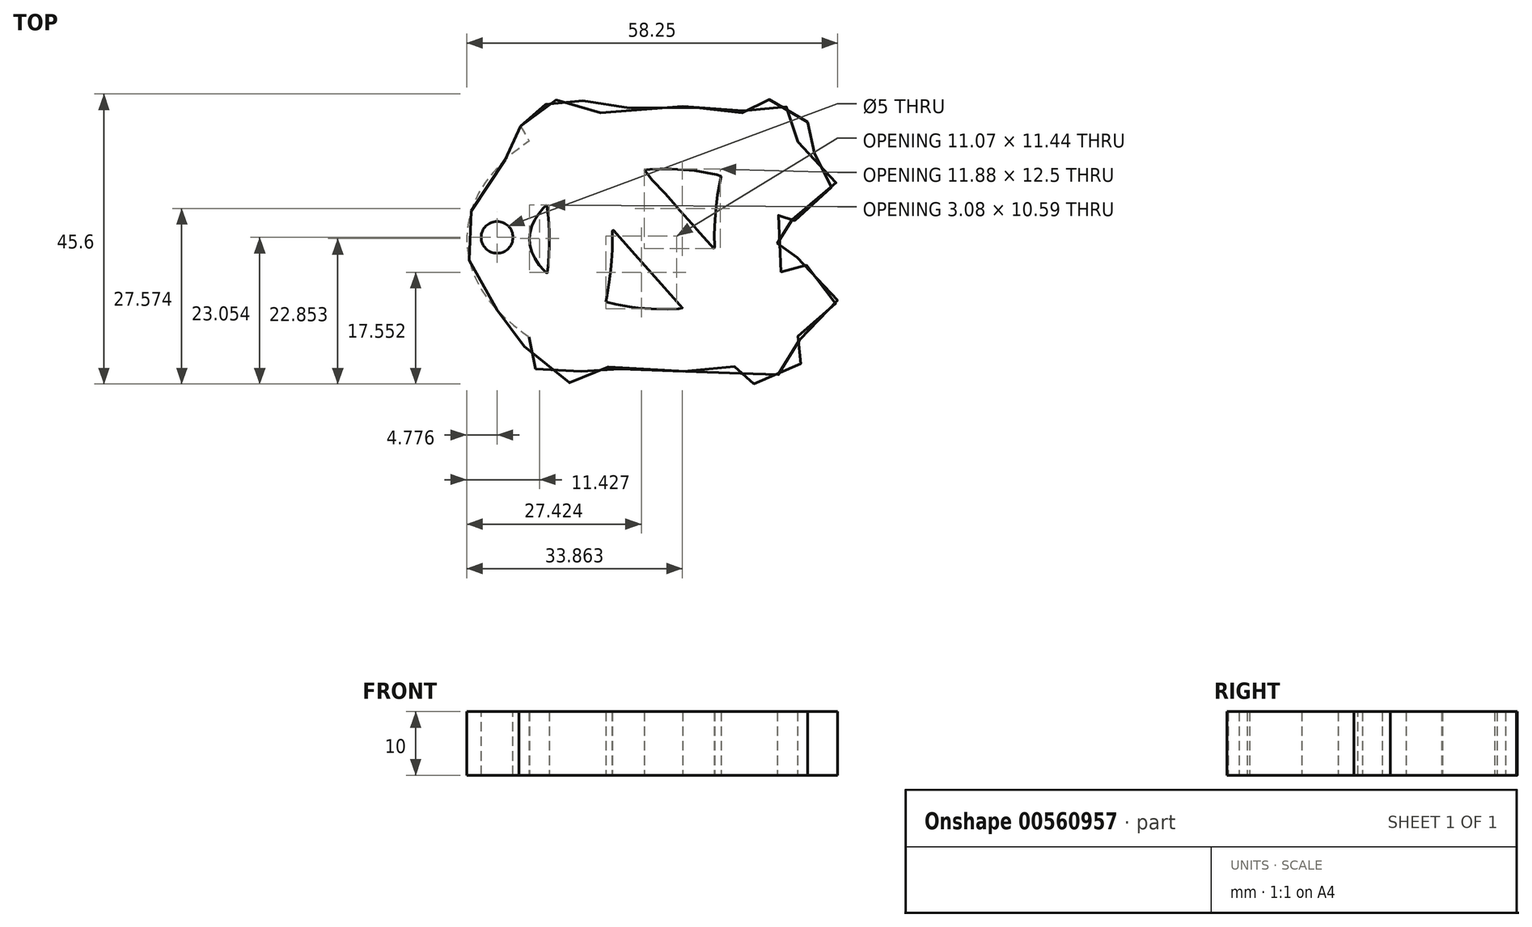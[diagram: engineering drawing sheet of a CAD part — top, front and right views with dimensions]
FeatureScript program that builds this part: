
annotation { "Feature Type Name" : "Feature", "Feature Type Description" : "" }
export const myFeature = defineFeature(function(context is Context, id is Id, definition is map)
    precondition{}
    {
        {
            var Q0;
            Q0=qCreatedBy(makeId("Top.planeOp"),FACE);
            var sketch = newSketch(context, id + "F0", { "sketchPlane" : qUnion([Q0])});
            skFitSpline(sketch, "E0", {"points": [v(22.56, 13.6) * mm, v(24.28, 13.2) * mm, v(26.83, 12.77) * mm, v(28.02, 12.64) * mm, v(32.02, 12.47) * mm, v(34.06, 12.57) * mm, v(34.53, 12.6) * mm, v(34.59, 12.65) * mm, v(34.37, 12.87) * mm, v(33.38, 13.98) * mm, v(32.2, 15.3) * mm, v(29.76, 18.07) * mm, v(28.72, 19.23) * mm, v(25.85, 22.49) * mm, v(23.63, 25) * mm, v(23.56, 25.06) * mm, v(23.51, 24.96) * mm, v(23.54, 24.73) * mm, v(23.53, 23.34) * mm, v(23.51, 21.7) * mm, v(23.39, 19.63) * mm, v(23.28, 18.47) * mm, v(22.87, 15.57) * mm, v(22.57, 13.83) * mm, v(22.56, 13.6) * mm]});
            skFitSpline(sketch, "E1", {"points": [v(28.6, 34.36) * mm, v(31.72, 30.78) * mm, v(32.9, 29.45) * mm, v(36.42, 25.48) * mm, v(37.9, 23.8) * mm, v(39.45, 22.04) * mm, v(39.53, 21.98) * mm, v(39.59, 21.98) * mm, v(39.59, 22.3) * mm, v(39.61, 25.62) * mm, v(39.91, 29.35) * mm, v(40.25, 31.57) * mm, v(40.6, 33.32) * mm, v(40.62, 33.43) * mm, v(40.24, 33.55) * mm, v(38.05, 34) * mm, v(35.63, 34.33) * mm, v(32.77, 34.53) * mm, v(30.36, 34.5) * mm, v(28.87, 34.45) * mm, v(28.6, 34.36) * mm]});
            skFitSpline(sketch, "E2", {"points": [v(9.14, 41.25) * mm, v(9.4, 40.84) * mm, v(9.78, 40.16) * mm, v(10.08, 39.61) * mm, v(10.38, 39) * mm, v(10.46, 38.86) * mm, v(10.35, 38.74) * mm, v(9.58, 38.22) * mm, v(8.8, 37.67) * mm, v(8, 37.07) * mm, v(6.93, 36.15) * mm, v(5.98, 35.25) * mm, v(4.6, 33.73) * mm, v(3.85, 32.8) * mm, v(3.18, 31.77) * mm, v(2.49, 30.58) * mm, v(2.03, 29.64) * mm, v(1.61, 28.58) * mm, v(1.18, 27.26) * mm, v(0.97, 26.42) * mm, v(0.77, 25.13) * mm, v(0.7, 24.4) * mm, v(0.7, 23.98) * mm, v(0.68, 23.85) * mm, v(0.7, 22.98) * mm, v(0.83, 21.5) * mm, v(0.9, 21.07) * mm, v(1.03, 20.32) * mm, v(1.38, 19.08) * mm, v(1.69, 18.25) * mm, v(2.12, 17.17) * mm, v(2.93, 15.65) * mm, v(3.38, 14.97) * mm, v(3.72, 14.43) * mm, v(4.53, 13.38) * mm, v(5.37, 12.41) * mm, v(6.6, 11.18) * mm, v(7.7, 10.2) * mm, v(8.13, 9.89) * mm, v(9.12, 9.1) * mm, v(9.74, 8.67) * mm, v(10.36, 8.29) * mm, v(10.47, 8.2) * mm, v(10.3, 7.85) * mm, v(9.98, 7.16) * mm, v(9.34, 6) * mm, v(9.03, 5.52) * mm, v(8.91, 5.1) * mm, v(9.06, 4.58) * mm, v(9.41, 4.23) * mm, v(12.7, 2.54) * mm, v(15.19, 1.49) * mm, v(16.83, 0.9) * mm, v(17.28, 0.92) * mm, v(17.6, 1.03) * mm, v(18.14, 1.78) * mm, v(18.92, 3.2) * mm, v(19.38, 4.2) * mm, v(19.41, 4.26) * mm, v(20.55, 3.92) * mm, v(21.12, 3.8) * mm, v(21.62, 3.7) * mm, v(23.49, 3.3) * mm, v(25.4, 3) * mm, v(29.12, 2.65) * mm, v(30.07, 2.6) * mm, v(32.43, 2.58) * mm, v(34.36, 2.67) * mm, v(35.25, 2.74) * mm, v(37.84, 3.02) * mm, v(40.53, 3.48) * mm, v(42.25, 3.86) * mm, v(42.32, 3.88) * mm, v(42.4, 3.84) * mm, v(42.44, 3.76) * mm, v(42.72, 3.48) * mm, v(42.85, 3.32) * mm, v(43.36, 2.75) * mm, v(43.5, 2.59) * mm, v(43.93, 2.1) * mm, v(44.09, 1.92) * mm, v(44.61, 1.35) * mm, v(44.81, 1.12) * mm, v(45, 0.92) * mm, v(45.24, 0.78) * mm, v(45.53, 0.7) * mm, v(45.85, 0.76) * mm, v(46.58, 1) * mm, v(47.24, 1.23) * mm, v(47.49, 1.32) * mm, v(49.43, 2.1) * mm, v(50.83, 2.72) * mm, v(53.05, 3.86) * mm, v(53.77, 4.28) * mm, v(54.01, 4.5) * mm, v(54.18, 4.84) * mm, v(54.16, 5.35) * mm, v(53.91, 5.82) * mm, v(53.43, 6.64) * mm, v(53.05, 7.36) * mm, v(52.67, 8.13) * mm, v(52.64, 8.17) * mm, v(53.65, 8.84) * mm, v(55.08, 9.91) * mm, v(56.03, 10.69) * mm, v(57.17, 11.77) * mm, v(57.97, 12.6) * mm, v(58.73, 13.52) * mm, v(58.91, 13.95) * mm, v(58.87, 14.37) * mm, v(58.45, 14.94) * mm, v(57.08, 16.3) * mm, v(55.6, 17.78) * mm, v(53.86, 19.52) * mm, v(53.23, 20.14) * mm, v(52.87, 20.48) * mm, v(52.82, 20.55) * mm, v(52.21, 20.64) * mm, v(51.84, 20.48) * mm, v(51.48, 20.12) * mm, v(51.12, 19.55) * mm, v(50.48, 18.8) * mm, v(49.87, 18.19) * mm, v(49.8, 18.16) * mm, v(49.77, 18.58) * mm, v(49.65, 19.88) * mm, v(49.48, 22.42) * mm, v(49.53, 25.99) * mm, v(49.73, 28.15) * mm, v(49.8, 28.75) * mm, v(49.83, 28.82) * mm, v(49.92, 28.77) * mm, v(50.42, 28.26) * mm, v(50.97, 27.61) * mm, v(51.3, 27.21) * mm, v(51.5, 26.87) * mm, v(51.73, 26.59) * mm, v(52.04, 26.45) * mm, v(52.33, 26.38) * mm, v(52.76, 26.46) * mm, v(53.26, 26.9) * mm, v(54.49, 28.12) * mm, v(54.9, 28.55) * mm, v(56.6, 30.25) * mm, v(58.22, 31.9) * mm, v(58.73, 32.4) * mm, v(58.9, 32.8) * mm, v(58.86, 33.21) * mm, v(58.04, 34.31) * mm, v(57.32, 35.1) * mm, v(56.05, 36.3) * mm, v(54.47, 37.58) * mm, v(53.48, 38.27) * mm, v(52.7, 38.78) * mm, v(52.65, 38.82) * mm, v(52.7, 38.94) * mm, v(53.3, 40.1) * mm, v(54.05, 41.42) * mm, v(54.21, 41.81) * mm, v(54.14, 42.3) * mm, v(54.01, 42.51) * mm, v(53.86, 42.67) * mm, v(53, 43.18) * mm, v(52.08, 43.67) * mm, v(50.32, 44.55) * mm, v(48.52, 45.32) * mm, v(46.93, 45.9) * mm, v(46.22, 46.13) * mm, v(45.73, 46.1) * mm, v(45.4, 45.93) * mm, v(45.25, 45.66) * mm, v(44.89, 45.12) * mm, v(44.44, 44.26) * mm, v(44.03, 43.47) * mm, v(43.7, 42.79) * mm, v(43.66, 42.77) * mm, v(43.2, 42.9) * mm, v(41.89, 43.24) * mm, v(40.49, 43.55) * mm, v(38.39, 43.92) * mm, v(36.3, 44.2) * mm, v(34.2, 44.36) * mm, v(32.48, 44.43) * mm, v(28.66, 44.37) * mm, v(26.5, 44.16) * mm, v(23.92, 43.8) * mm, v(22.43, 43.5) * mm, v(20.83, 43.13) * mm, v(20.76, 43.14) * mm, v(20.67, 43.23) * mm, v(19.7, 44.35) * mm, v(18.58, 45.61) * mm, v(18.13, 46.11) * mm, v(17.86, 46.25) * mm, v(17.44, 46.3) * mm, v(16.63, 46.04) * mm, v(14.84, 45.4) * mm, v(13.8, 44.98) * mm, v(12.85, 44.55) * mm, v(11.75, 44.02) * mm, v(10.6, 43.44) * mm, v(9.56, 42.85) * mm, v(9.2, 42.65) * mm, v(9.04, 42.41) * mm, v(8.93, 42.08) * mm, v(8.96, 41.7) * mm, v(9.14, 41.25) * mm]});
            skFitSpline(sketch, "E3", {"points": [v(13.25, 28.86) * mm, v(13.3, 28.73) * mm, v(13.38, 28) * mm, v(13.44, 27.38) * mm, v(13.55, 26.24) * mm, v(13.62, 24.54) * mm, v(13.64, 22.66) * mm, v(13.57, 20.64) * mm, v(13.36, 18.57) * mm, v(13.3, 18.2) * mm, v(13.28, 18.16) * mm, v(13.05, 18.34) * mm, v(11.98, 19.54) * mm, v(11.06, 21.08) * mm, v(10.58, 22.84) * mm, v(10.6, 24.32) * mm, v(10.92, 25.55) * mm, v(11.62, 26.91) * mm, v(12.71, 28.34) * mm, v(13.25, 28.86) * mm]});
            skSolve(sketch);
        }
        {
            var Q0;
            Q0=makeQuery(id+"F0.imprint","IMPRINT",FACE,{"disambiguationData":[TD([[makeQuery(id+"F0.imprint","IMPRINT",EDGE,{"derivedFrom":sQuery(id+"F0.wireOp",EDGE,"E0")}),-1.0]])]});
            extrude(context, id + "F1", {"entities" : qUnion([Q0]), "depth" : 10 * mm, "offsetDistance" : 25 * mm});
        }
        {
            var Q0;
            Q0=makeQuery(id+"F1.opExtrude","CAP_FACE",FACE,{"disambiguationData":[OSD([sQuery(id+"F0.wireOp",EDGE,"E0"),sQuery(id+"F0.wireOp",EDGE,"E1"),sQuery(id+"F0.wireOp",EDGE,"E2"),sQuery(id+"F0.wireOp",EDGE,"E3")])],"isStart":false});
            var sketch = newSketch(context, id + "F2", { "sketchPlane" : qUnion([Q0])});
            skCircle(sketch, "E4", {"center": v(5.45, 23.76) * mm, "radius": 2.5 * mm});
            skSolve(sketch);
        }
        {
            var Q0;
            Q0=makeQuery(id+"F2.imprint","IMPRINT",FACE,{"disambiguationData":[TD([[makeQuery(id+"F2.imprint","IMPRINT",EDGE,{"derivedFrom":sQuery(id+"F2.wireOp",EDGE,"E4")}),1.0]])]});
            extrude(context, id + "F3", {"entities" : qUnion([Q0]), "operationType" : NewBodyOperationType.REMOVE, "oppositeDirection" : true, "depth" : 25 * mm, "offsetDistance" : 25 * mm});
        }
    });
